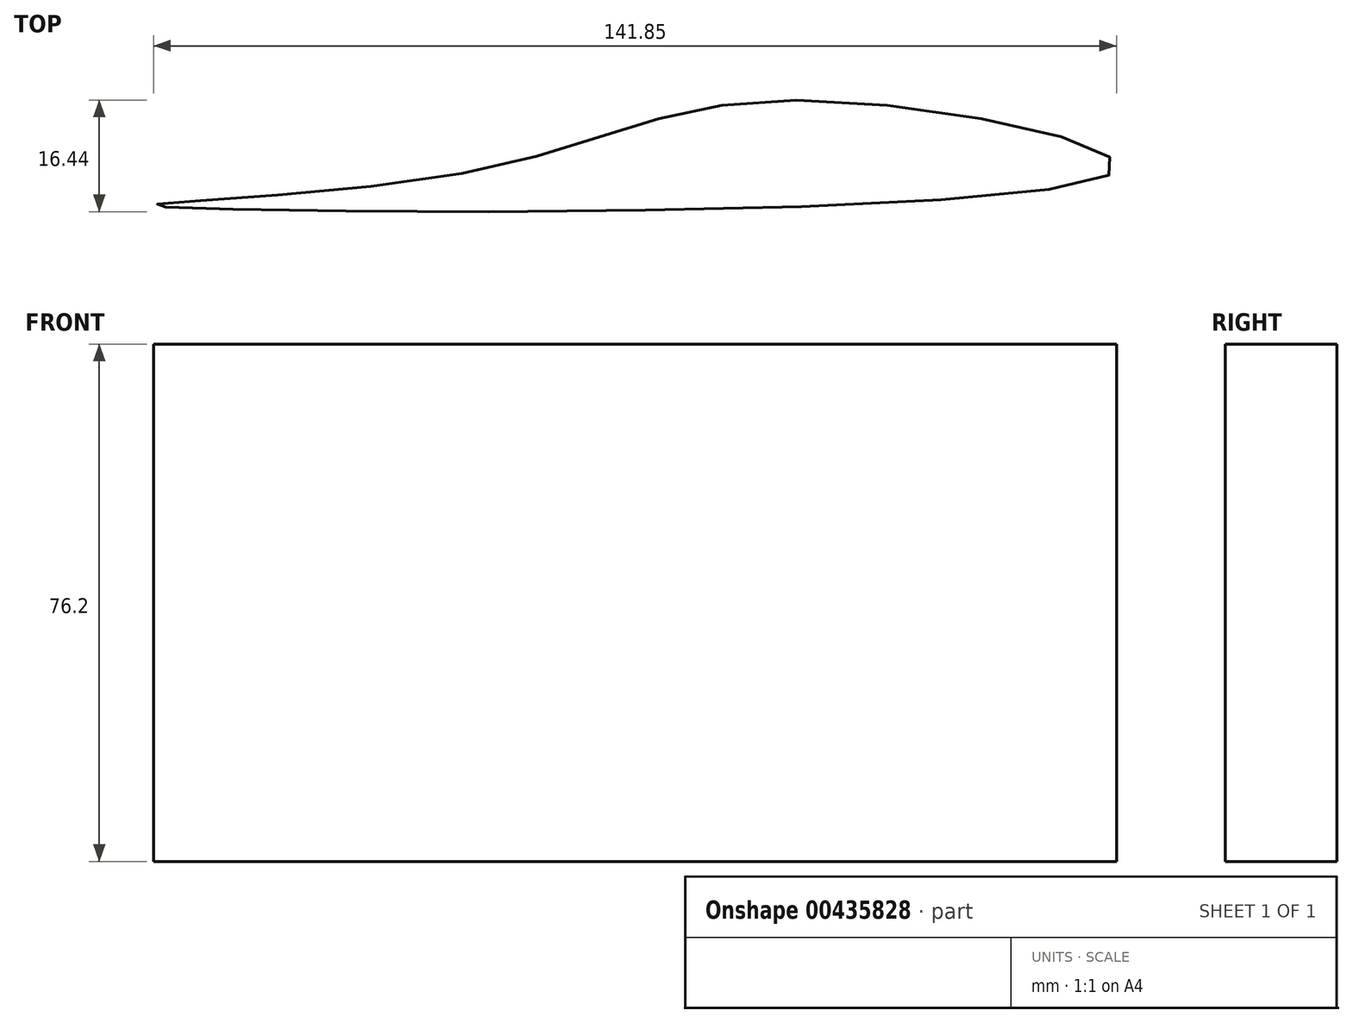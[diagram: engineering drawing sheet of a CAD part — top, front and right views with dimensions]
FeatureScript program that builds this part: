
annotation { "Feature Type Name" : "Feature", "Feature Type Description" : "" }
export const myFeature = defineFeature(function(context is Context, id is Id, definition is map)
    precondition{}
    {
        {
            var Q0;
            Q0=qCreatedBy(makeId("Top.planeOp"),FACE);
            var sketch = newSketch(context, id + "F0", { "sketchPlane" : qUnion([Q0])});
            skFitSpline(sketch, "E0", {"points": [v(-33.3, 0) * mm, v(16.46, 10.83) * mm, v(62.48, 0) * mm, v(-78.08, -4.82) * mm, v(-33.3, 0) * mm]});
            skSolve(sketch);
        }
        {
            var Q0;
            Q0=sQuery(id+"F0.wireOp",EDGE,"E0");
            extrude(context, id + "F1", {"bodyType" : ToolBodyType.SURFACE, "surfaceEntities" : qUnion([Q0]), "depth" : 76.2 * mm});
        }
    });
